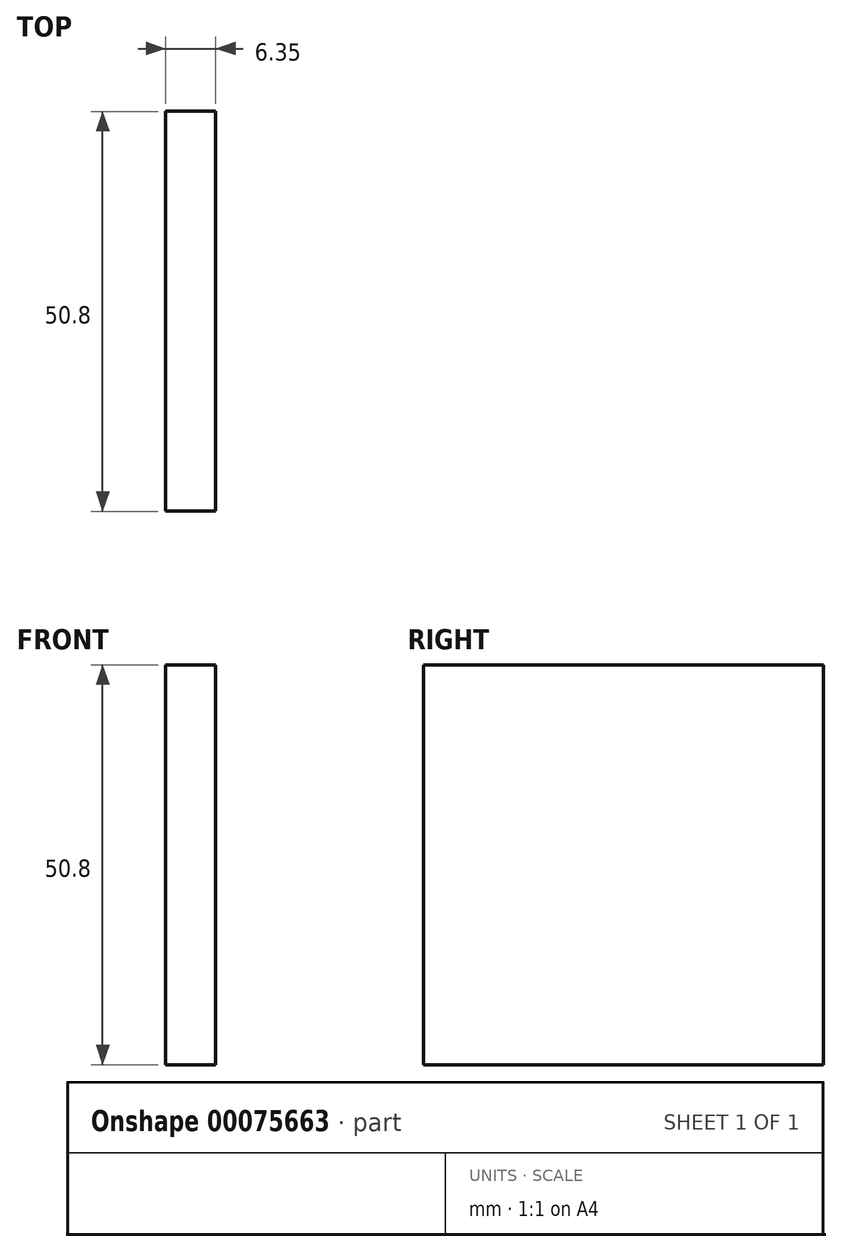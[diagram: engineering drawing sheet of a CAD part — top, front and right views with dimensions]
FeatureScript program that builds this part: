
annotation { "Feature Type Name" : "Feature", "Feature Type Description" : "" }
export const myFeature = defineFeature(function(context is Context, id is Id, definition is map)
    precondition{}
    {
        {
            var Q0;
            Q0=qCreatedBy(makeId("Right.planeOp"),FACE);
            var sketch = newSketch(context, id + "F0", { "sketchPlane" : qUnion([Q0])});
            skLineSegment(sketch, "E0.bottom", {"start": v(-54.44, 26.98) * mm, "end": v(-3.64, 26.98) * mm});
            skLineSegment(sketch, "E0.top", {"start": v(-54.44, -23.82) * mm, "end": v(-3.64, -23.82) * mm});
            skLineSegment(sketch, "E0.left", {"start": v(-54.44, 26.98) * mm, "end": v(-54.44, -23.82) * mm});
            skLineSegment(sketch, "E0.right", {"start": v(-3.64, 26.98) * mm, "end": v(-3.64, -23.82) * mm});
            skSolve(sketch);
        }
        {
            var Q0;
            Q0=makeQuery(id+"F0.imprint","IMPRINT",FACE,{"disambiguationData":[TD([[makeQuery(id+"F0.imprint","IMPRINT",EDGE,{"derivedFrom":sQuery(id+"F0.wireOp",EDGE,"E0.bottom")}),-1.0]])]});
            extrude(context, id + "F1", {"entities" : qUnion([Q0]), "depth" : 6.35 * mm});
        }
    });
